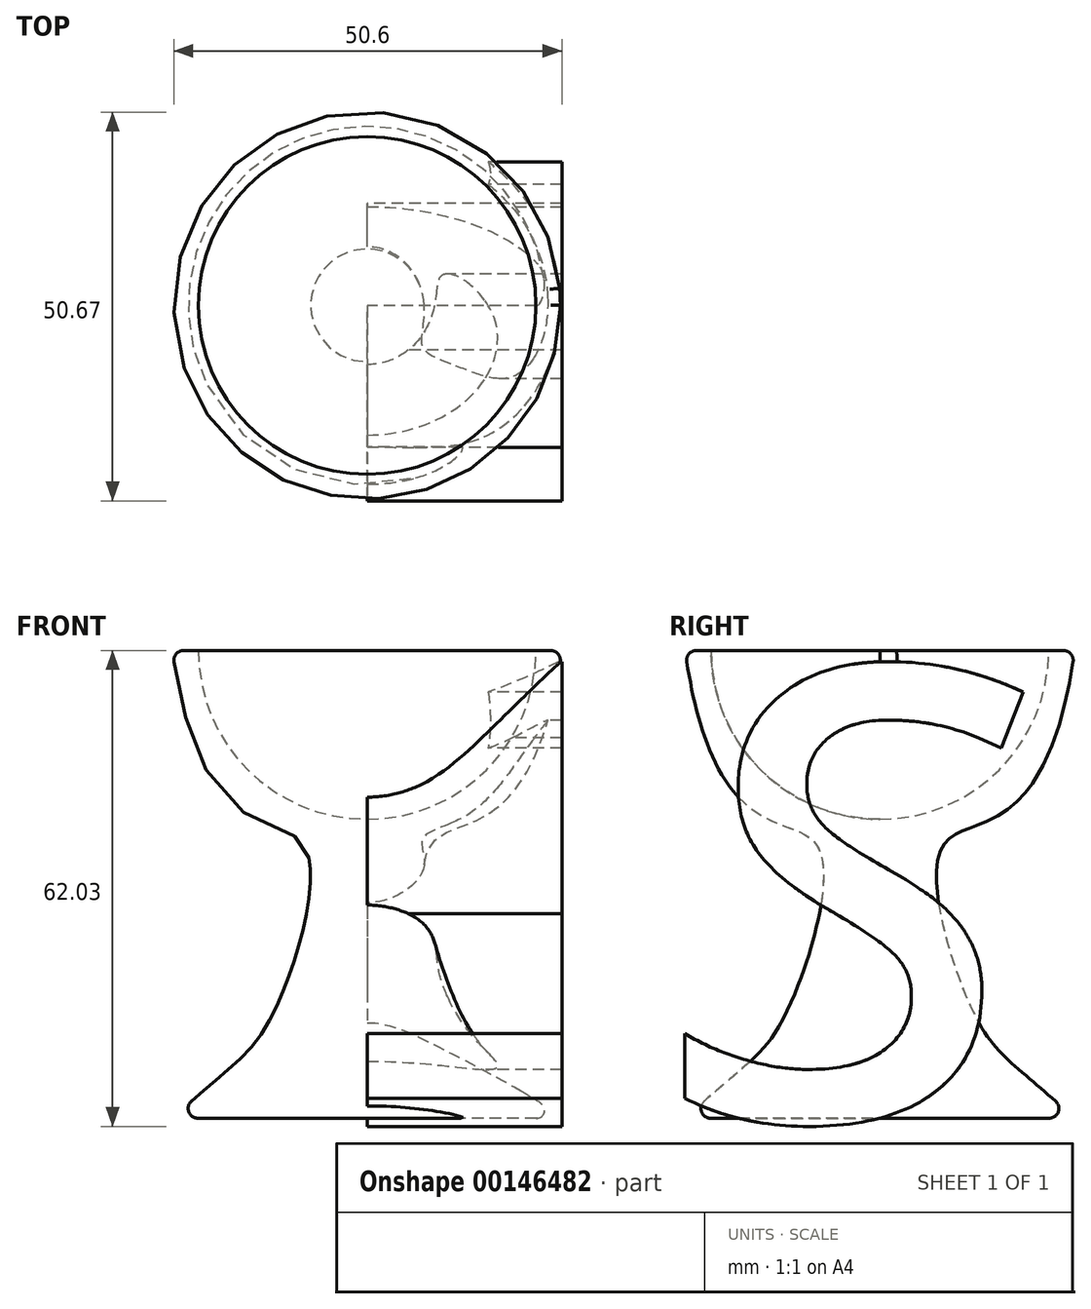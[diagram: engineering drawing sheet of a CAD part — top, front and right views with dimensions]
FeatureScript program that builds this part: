
annotation { "Feature Type Name" : "Feature", "Feature Type Description" : "" }
export const myFeature = defineFeature(function(context is Context, id is Id, definition is map)
    precondition{}
    {
        {
            var Q0;
            Q0=qCreatedBy(makeId("Top.planeOp"),FACE);
            var sketch = newSketch(context, id + "F0", { "sketchPlane" : qUnion([Q0])});
            skCircle(sketch, "E0", {"center": v(0, 0) * mm, "radius": 25.4 * mm});
            skSolve(sketch);
        }
        {
            var Q0;
            Q0 = qSketchRegion(id + "F0", true);
            extrude(context, id + "F1", {"entities" : qUnion([Q0]), "depth" : 60.96 * mm});
        }
        {
            var Q0;
            Q0=qCreatedBy(makeId("Right.planeOp"),FACE);
            var sketch = newSketch(context, id + "F2", { "sketchPlane" : qUnion([Q0])});
            skLineSegment(sketch, "E1", {"start": v(-25.4, 68.11) * mm, "end": v(-25.4, -17.35) * mm});
            skLineSegment(sketch, "E2", {"start": v(0, 72.67) * mm, "end": v(0, -28.26) * mm, "construction": true});
            skLineSegment(sketch, "E3", {"start": v(-56.9, 60.96) * mm, "end": v(70.99, 60.96) * mm, "construction": true});
            skFitSpline(sketch, "E4", {"points": [v(-25.4, 60.96) * mm, v(-8.13, 35.4) * mm, v(-12.3, 13.58) * mm, v(-25.4, 0) * mm], "startDerivative": vector(28.8, -208.4) * mm, "endDerivative": vector(-80.22, -73.02) * mm});
            skLineSegment(sketch, "E5", {"start": v(-25.4, 60.96) * mm, "end": v(-25.4, 0) * mm});
            skSolve(sketch);
        }
        {
            var Q0;
            Q0 = qSketchRegion(id + "F2", true);
            var Q1;
            Q1=sQuery(id+"F2.wireOp",EDGE,"E2");
            revolve(context, id + "F3", {"operationType" : NewBodyOperationType.REMOVE, "entities" : qUnion([Q0]), "axis" : qUnion([Q1]), "revolveType" : RevolveType.FULL, "oppositeDirection" : true});
        }
        {
            var Q0;
            Q0=qCreatedBy(makeId("Right.planeOp"),FACE);
            var sketch = newSketch(context, id + "F4", { "sketchPlane" : qUnion([Q0])});
            skText(sketch, "E6", { "text": "s", "fontName": "OpenSans-Italic.ttf"});
            const initialGuessF4  = {"E6": [-0.0259, 0, 1, 0, 0.07862]};
            skSetInitialGuess(sketch, initialGuessF4);
            skSolve(sketch);
        }
        {
            var Q0;
            Q0 = qSketchRegion(id + "F4", true);
            extrude(context, id + "F5", {"entities" : qUnion([Q0]), "operationType" : NewBodyOperationType.ADD, "depth" : 25.4 * mm});
        }
        {
            var Q0;
            Q0=qCreatedBy(makeId("Right.planeOp"),FACE);
            var sketch = newSketch(context, id + "F6", { "sketchPlane" : qUnion([Q0])});
            skArc(sketch, "E7", {"start": v(0, 38.96) * mm, "mid": v(22.01, 60.97) * mm, "end": v(0, 82.98) * mm});
            skLineSegment(sketch, "E8", {"start": v(0, 82.98) * mm, "end": v(0, 38.96) * mm});
            skSolve(sketch);
        }
        {
            var Q0;
            Q0 = qSketchRegion(id + "F6", true);
            var Q1;
            Q1=sQuery(id+"F6.wireOp",EDGE,"E8");
            revolve(context, id + "F7", {"operationType" : NewBodyOperationType.REMOVE, "entities" : qUnion([Q0]), "axis" : qUnion([Q1]), "revolveType" : RevolveType.FULL});
        }
        {
            var Q0;
            {var subQ0=sQuery(id+"F2.wireOp",EDGE,"E5");var subQ1=sQuery(id+"F2.wireOp",EDGE,"E4");Q0=makeQuery(id+"F3.boolean.opBoolean","MERGE",EDGE,{"derivedFrom":[makeQuery(id+"F1.opExtrude","CAP_EDGE",EDGE,{"disambiguationData":[OSD([sQuery(id+"F0.wireOp",EDGE,"E0")])],"isStart":false}),makeQuery(id+"F3.opRevolve","SWEPT_EDGE",EDGE,{"disambiguationData":[OSD([subQ1,subQ0]),TDD([makeQuery(id+"F2.imprint","INTERSECT",VERTEX,{"disambiguationData":[OD(0.0)],"derivedFrom":[subQ1,subQ0]})])]})]});}
            var Q1;
            {var subQ0=sQuery(id+"F2.wireOp",EDGE,"E5");var subQ1=sQuery(id+"F2.wireOp",EDGE,"E4");Q1=makeQuery(id+"F3.boolean.opBoolean","MERGE",EDGE,{"derivedFrom":[makeQuery(id+"F1.opExtrude","CAP_EDGE",EDGE,{"disambiguationData":[OSD([sQuery(id+"F0.wireOp",EDGE,"E0")])],"isStart":true}),makeQuery(id+"F3.opRevolve","SWEPT_EDGE",EDGE,{"disambiguationData":[OSD([subQ1,subQ0]),TDD([makeQuery(id+"F2.imprint","INTERSECT",VERTEX,{"disambiguationData":[OD(1.0)],"derivedFrom":[subQ1,subQ0]})])]})]});}
            fillet(context, id + "F8", {"entities" : qUnion([Q0, Q1]), "radius" : 1.27 * mm, "tangentPropagation" : true, "allowEdgeOverflow" : false});
        }
    });
